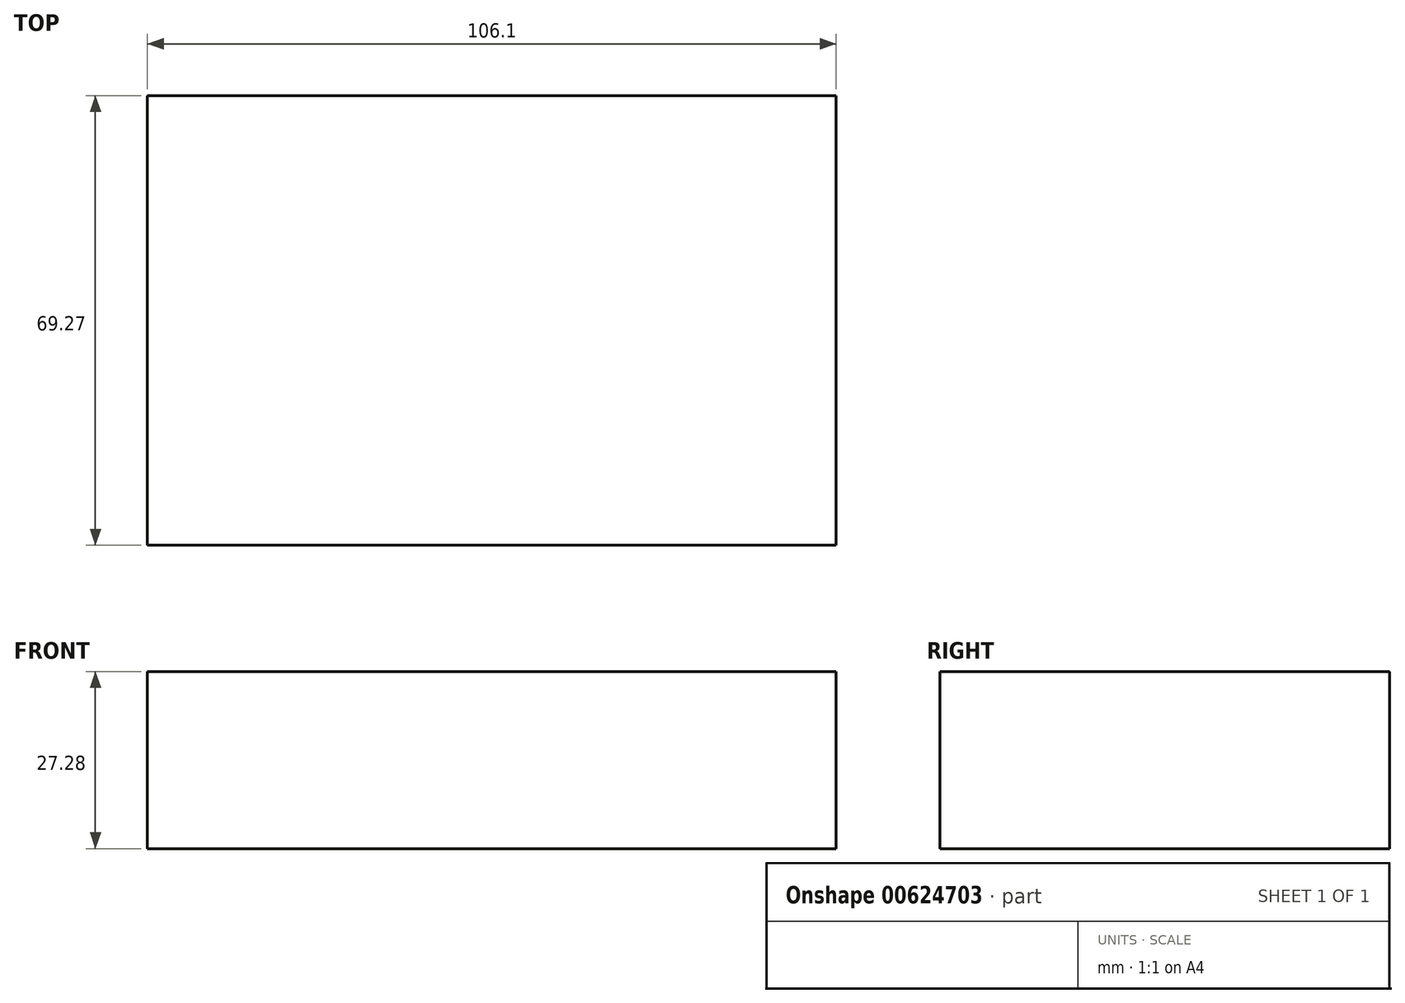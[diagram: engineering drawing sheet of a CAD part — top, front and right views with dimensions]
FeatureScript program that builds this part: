
annotation { "Feature Type Name" : "Feature", "Feature Type Description" : "" }
export const myFeature = defineFeature(function(context is Context, id is Id, definition is map)
    precondition{}
    {
        {
            var Q0;
            Q0=qCreatedBy(makeId("Front.planeOp"),FACE);
            var sketch = newSketch(context, id + "F0", { "sketchPlane" : qUnion([Q0])});
            skLineSegment(sketch, "E0.bottom", {"start": v(-71.66, 40.9) * mm, "end": v(34.44, 40.9) * mm});
            skLineSegment(sketch, "E0.top", {"start": v(-71.66, 68.17) * mm, "end": v(34.44, 68.17) * mm});
            skLineSegment(sketch, "E0.left", {"start": v(-71.66, 40.9) * mm, "end": v(-71.66, 68.17) * mm});
            skLineSegment(sketch, "E0.right", {"start": v(34.44, 40.9) * mm, "end": v(34.44, 68.17) * mm});
            skSolve(sketch);
        }
        {
            var Q0;
            Q0 = qSketchRegion(id + "F0", true);
            extrude(context, id + "F1", {"entities" : qUnion([Q0]), "depth" : 69.27 * mm, "offsetDistance" : 25.4 * mm});
        }
        {
            var Q0;
            Q0=makeQuery(id+"F1.opExtrude","SWEPT_FACE",FACE,{"disambiguationData":[OSD([sQuery(id+"F0.wireOp",EDGE,"E0.top")])]});
            var sketch = newSketch(context, id + "F2", { "sketchPlane" : qUnion([Q0])});
            skCircle(sketch, "E1", {"center": v(-26.9, -43.02) * mm, "radius": 18.7 * mm});
            skSolve(sketch);
        }
        {
            var Q0;
            Q0=sQuery(id+"F2.wireOp",EDGE,"E1");
            extrude(context, id + "F3", {"bodyType" : ToolBodyType.SURFACE, "surfaceEntities" : qUnion([Q0]), "depth" : 25.4 * mm, "offsetDistance" : 25.4 * mm});
        }
    });
